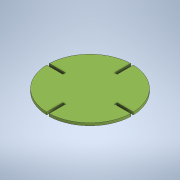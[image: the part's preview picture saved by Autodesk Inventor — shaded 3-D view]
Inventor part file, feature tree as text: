
AUTODESK INVENTOR PART (.ipt)
format: ipt  version: 2021 (Build 250183000, 183)  size: 133,632 bytes
history: native  units: in
note: dims shown in document units (in); Inventor stores cm internally (conversion verified against a paired STEP export)
features: sketch x2, extrude x1
ambient origin geometry x8: Origin, YZ Plane, XZ Plane, XY Plane, X Axis, Y Axis, Z Axis, Center Point
bodies: Solid1 (feature_tree)
feature tree (3):
  sketch  "Sketch1"  dims[d2=0.0315in d3=0.0315in]
  extrude  "Extrusion1"  Depth=0.0315in
  sketch  "Sketch2"  dims[d4=0.0315in d5=0.0315in d6=1.2598in d7=0.0in d8=0.0in d9=2.0472in d10=0.0in d11=0.0in d12=0.0in d13=0.063in d14=0.0in]
